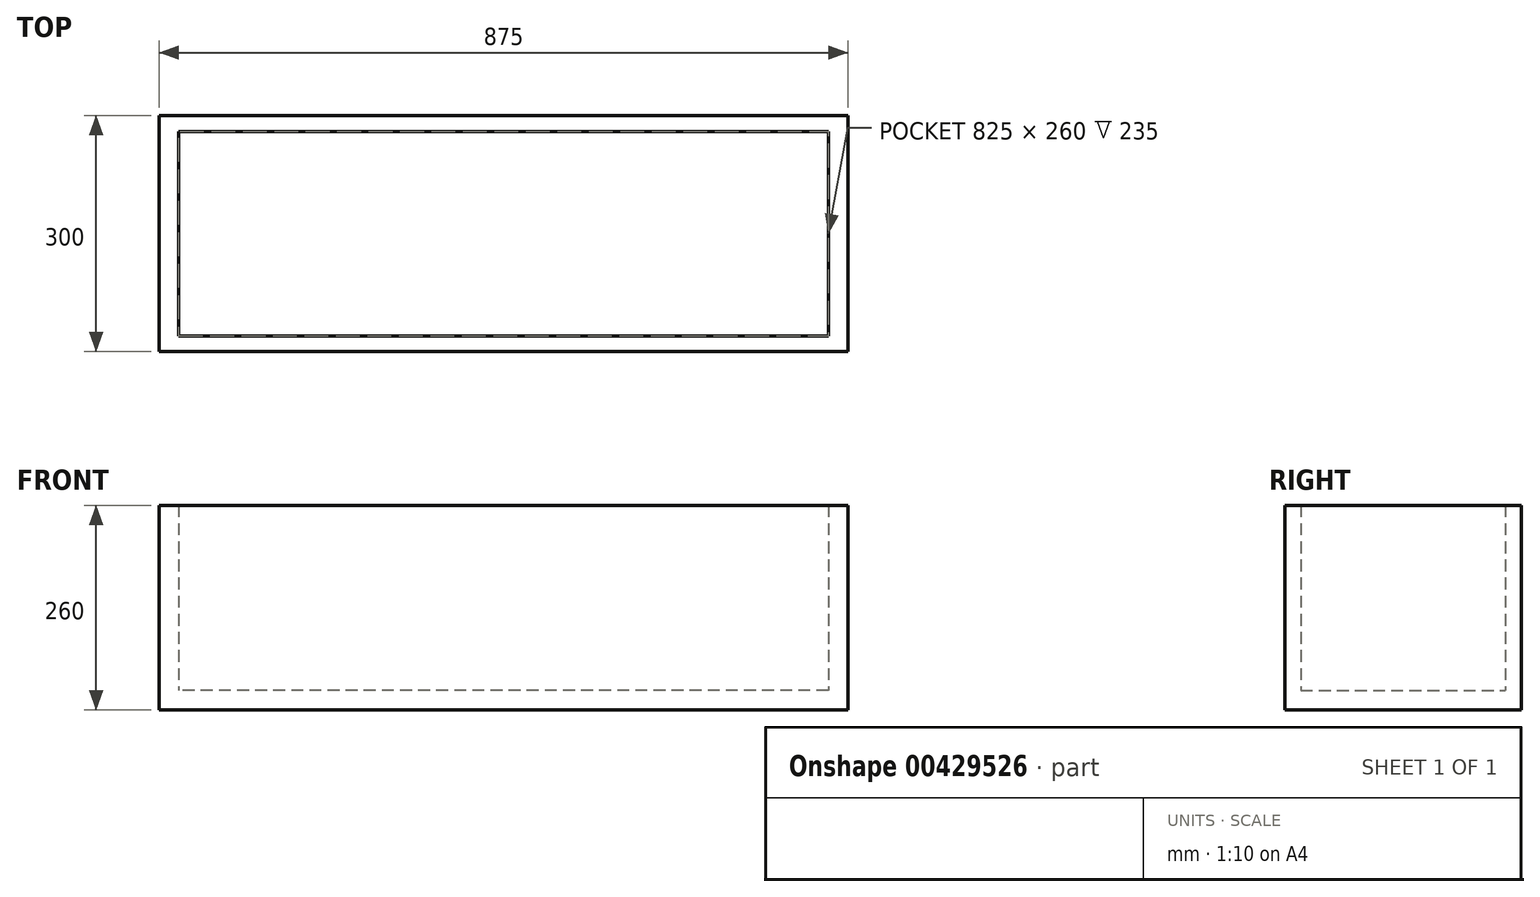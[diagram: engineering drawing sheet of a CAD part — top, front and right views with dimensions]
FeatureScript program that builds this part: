
annotation { "Feature Type Name" : "Feature", "Feature Type Description" : "" }
export const myFeature = defineFeature(function(context is Context, id is Id, definition is map)
    precondition{}
    {
        {
            var Q0;
            Q0=qCreatedBy(makeId("Top.planeOp"),FACE);
            var sketch = newSketch(context, id + "F0", { "sketchPlane" : qUnion([Q0])});
            skLineSegment(sketch, "E0.bottom", {"start": v(447.5, -150) * mm, "end": v(-427.5, -150) * mm});
            skLineSegment(sketch, "E0.top", {"start": v(447.5, 150) * mm, "end": v(-427.5, 150) * mm});
            skLineSegment(sketch, "E0.left", {"start": v(447.5, -150) * mm, "end": v(447.5, 150) * mm});
            skLineSegment(sketch, "E0.right", {"start": v(-427.5, -150) * mm, "end": v(-427.5, 150) * mm});
            skPoint(sketch, "E0.middle", {"position": v(0, 0) * mm});
            skLineSegment(sketch, "E1.0", {"start": v(-402.5, -150) * mm, "end": v(-402.5, 150) * mm});
            skLineSegment(sketch, "E2.0", {"start": v(422.5, -130) * mm, "end": v(-402.5, -130) * mm});
            skLineSegment(sketch, "E3.0", {"start": v(422.5, -150) * mm, "end": v(422.5, 150) * mm});
            skLineSegment(sketch, "E4.0", {"start": v(422.5, 130) * mm, "end": v(-402.5, 130) * mm});
            skPoint(sketch, "E5.orphan", {"position": v(427.5, 150) * mm});
            skPoint(sketch, "E6.orphan", {"position": v(427.5, -150) * mm});
            skSolve(sketch);
        }
        {
            var Q0;
            {var subQ0=sQuery(id+"F0.wireOp",EDGE,"E2.0");var subQ1=sQuery(id+"F0.wireOp",EDGE,"E0.right");var subQ2=makeQuery(id+"F0.imprint","INTERSECT",VERTEX,{"derivedFrom":[subQ1,subQ0]});Q0=makeQuery(id+"F0.imprint","IMPRINT",FACE,{"disambiguationData":[TD([[makeQuery(id+"F0.imprint","IMPRINT",EDGE,{"disambiguationData":[TD([[subQ2,-1.0]])],"derivedFrom":subQ1}),-1.0]])]});}
            var Q1;
            {var subQ0=sQuery(id+"F0.wireOp",EDGE,"E1.0");var subQ1=sQuery(id+"F0.wireOp",EDGE,"E0.top");var subQ2=makeQuery(id+"F0.imprint","INTERSECT",VERTEX,{"derivedFrom":[subQ1,subQ0]});Q1=makeQuery(id+"F0.imprint","IMPRINT",FACE,{"disambiguationData":[TD([[makeQuery(id+"F0.imprint","IMPRINT",EDGE,{"disambiguationData":[TD([[subQ2,1.0]])],"derivedFrom":subQ1}),1.0]])]});}
            var Q2;
            {var subQ0=sQuery(id+"F0.wireOp",EDGE,"E2.0");var subQ1=sQuery(id+"F0.wireOp",EDGE,"E0.left");var subQ2=makeQuery(id+"F0.imprint","INTERSECT",VERTEX,{"derivedFrom":[subQ1,subQ0]});Q2=makeQuery(id+"F0.imprint","IMPRINT",FACE,{"disambiguationData":[TD([[makeQuery(id+"F0.imprint","IMPRINT",EDGE,{"disambiguationData":[TD([[subQ2,-1.0]])],"derivedFrom":subQ1}),1.0]])]});}
            var Q3;
            {var subQ0=sQuery(id+"F0.wireOp",EDGE,"E0.left");var subQ1=sQuery(id+"F0.wireOp",EDGE,"E0.top");var subQ2=makeQuery(id+"F0.imprint","INTERSECT",VERTEX,{"derivedFrom":[subQ1,subQ0]});Q3=makeQuery(id+"F0.imprint","IMPRINT",FACE,{"disambiguationData":[TD([[makeQuery(id+"F0.imprint","IMPRINT",EDGE,{"disambiguationData":[TD([[subQ2,-1.0]])],"derivedFrom":subQ1}),1.0]])]});}
            var Q4;
            {var subQ0=sQuery(id+"F0.wireOp",EDGE,"E1.0");var subQ1=sQuery(id+"F0.wireOp",EDGE,"E0.bottom");var subQ2=makeQuery(id+"F0.imprint","INTERSECT",VERTEX,{"derivedFrom":[subQ1,subQ0]});Q4=makeQuery(id+"F0.imprint","IMPRINT",FACE,{"disambiguationData":[TD([[makeQuery(id+"F0.imprint","IMPRINT",EDGE,{"disambiguationData":[TD([[subQ2,1.0]])],"derivedFrom":subQ1}),-1.0]])]});}
            var Q5;
            {var subQ0=sQuery(id+"F0.wireOp",EDGE,"E0.right");var subQ1=sQuery(id+"F0.wireOp",EDGE,"E0.bottom");var subQ2=makeQuery(id+"F0.imprint","INTERSECT",VERTEX,{"derivedFrom":[subQ1,subQ0]});Q5=makeQuery(id+"F0.imprint","IMPRINT",FACE,{"disambiguationData":[TD([[makeQuery(id+"F0.imprint","IMPRINT",EDGE,{"disambiguationData":[TD([[subQ2,1.0]])],"derivedFrom":subQ1}),-1.0]])]});}
            var Q6;
            {var subQ0=sQuery(id+"F0.wireOp",EDGE,"E0.left");var subQ1=sQuery(id+"F0.wireOp",EDGE,"E0.bottom");var subQ2=makeQuery(id+"F0.imprint","INTERSECT",VERTEX,{"derivedFrom":[subQ1,subQ0]});Q6=makeQuery(id+"F0.imprint","IMPRINT",FACE,{"disambiguationData":[TD([[makeQuery(id+"F0.imprint","IMPRINT",EDGE,{"disambiguationData":[TD([[subQ2,-1.0]])],"derivedFrom":subQ1}),-1.0]])]});}
            var Q7;
            {var subQ0=sQuery(id+"F0.wireOp",EDGE,"E0.right");var subQ1=sQuery(id+"F0.wireOp",EDGE,"E0.top");var subQ2=makeQuery(id+"F0.imprint","INTERSECT",VERTEX,{"derivedFrom":[subQ1,subQ0]});Q7=makeQuery(id+"F0.imprint","IMPRINT",FACE,{"disambiguationData":[TD([[makeQuery(id+"F0.imprint","IMPRINT",EDGE,{"disambiguationData":[TD([[subQ2,1.0]])],"derivedFrom":subQ1}),1.0]])]});}
            extrude(context, id + "F1", {"entities" : qUnion([Q0, Q1, Q2, Q3, Q4, Q5, Q6, Q7]), "depth" : 260 * mm});
        }
        {
            var Q0;
            {var subQ0=sQuery(id+"F0.wireOp",EDGE,"E2.0");var subQ1=sQuery(id+"F0.wireOp",EDGE,"E1.0");var subQ2=makeQuery(id+"F0.imprint","INTERSECT",VERTEX,{"derivedFrom":[subQ1,subQ0]});Q0=makeQuery(id+"F0.imprint","IMPRINT",FACE,{"disambiguationData":[TD([[makeQuery(id+"F0.imprint","IMPRINT",EDGE,{"disambiguationData":[TD([[subQ2,-1.0]])],"derivedFrom":subQ1}),-1.0]])]});}
            extrude(context, id + "F2", {"entities" : qUnion([Q0]), "operationType" : NewBodyOperationType.ADD, "depth" : 25 * mm});
        }
    });
